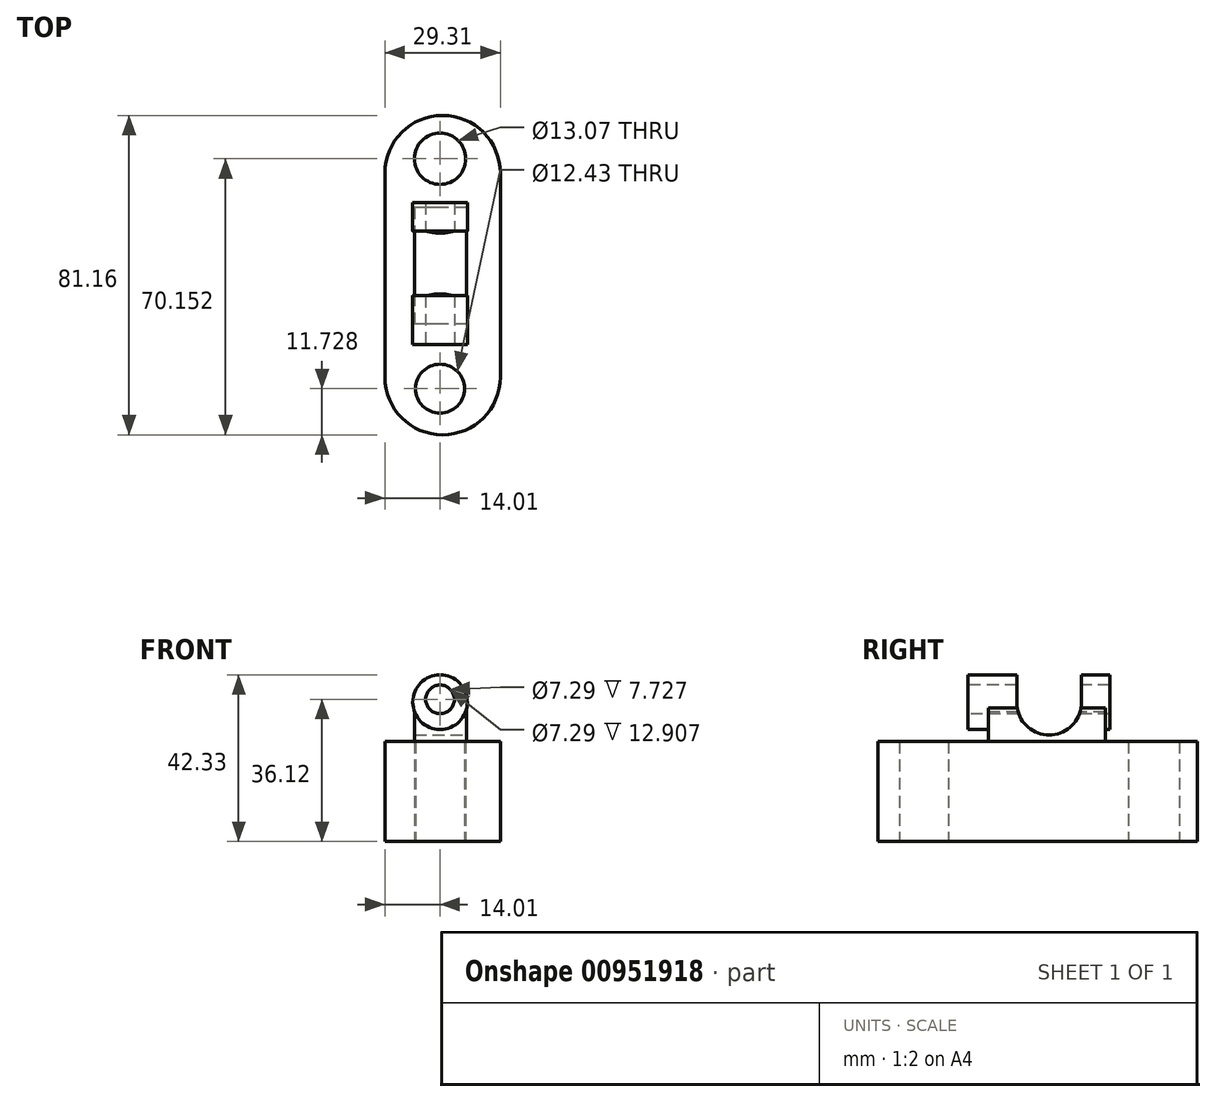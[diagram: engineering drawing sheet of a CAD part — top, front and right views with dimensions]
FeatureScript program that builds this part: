
annotation { "Feature Type Name" : "Feature", "Feature Type Description" : "" }
export const myFeature = defineFeature(function(context is Context, id is Id, definition is map)
    precondition{}
    {
        {
            var Q0;
            Q0=qCreatedBy(makeId("Top.planeOp"),FACE);
            var sketch = newSketch(context, id + "F0", { "sketchPlane" : qUnion([Q0])});
            skLineSegment(sketch, "E0.bottom", {"start": v(-14, -26.29) * mm, "end": v(15.3, -26.29) * mm});
            skLineSegment(sketch, "E0.top", {"start": v(-14, 25.56) * mm, "end": v(15.3, 25.56) * mm});
            skLineSegment(sketch, "E0.left", {"start": v(-14, -26.29) * mm, "end": v(-14, 25.56) * mm});
            skLineSegment(sketch, "E0.right", {"start": v(15.3, -26.29) * mm, "end": v(15.3, 25.56) * mm});
            skArc(sketch, "E1", {"start": v(-14, -26.29) * mm, "mid": v(0.64, -40.94) * mm, "end": v(15.3, -26.29) * mm});
            skArc(sketch, "E2", {"start": v(15.3, 25.56) * mm, "mid": v(0.64, 40.22) * mm, "end": v(-14, 25.56) * mm});
            skSolve(sketch);
        }
        {
            var Q0;
            Q0 = qSketchRegion(id + "F0", true);
            extrude(context, id + "F1", {"entities" : qUnion([Q0]), "depth" : 25.4 * mm, "offsetDistance" : 25.4 * mm});
        }
        {
            var Q0;
            Q0=qCreatedBy(makeId("Top.planeOp"),FACE);
            var sketch = newSketch(context, id + "F2", { "sketchPlane" : qUnion([Q0])});
            skCircle(sketch, "E3", {"center": v(0, -29.21) * mm, "radius": 6.21 * mm});
            skCircle(sketch, "E4", {"center": v(0, 29.21) * mm, "radius": 6.53 * mm});
            skSolve(sketch);
        }
        {
            var Q0;
            Q0=makeQuery(id+"F2.imprint","IMPRINT",FACE,{"disambiguationData":[TD([[makeQuery(id+"F2.imprint","IMPRINT",EDGE,{"derivedFrom":sQuery(id+"F2.wireOp",EDGE,"E3")}),1.0]])]});
            var Q1;
            Q1=makeQuery(id+"F2.imprint","IMPRINT",FACE,{"disambiguationData":[TD([[makeQuery(id+"F2.imprint","IMPRINT",EDGE,{"derivedFrom":sQuery(id+"F2.wireOp",EDGE,"E4")}),1.0]])]});
            extrude(context, id + "F3", {"entities" : qUnion([Q0, Q1]), "operationType" : NewBodyOperationType.REMOVE, "depth" : 73.9 * mm, "offsetDistance" : 25.4 * mm});
        }
        {
            var Q0;
            Q0=qCreatedBy(makeId("Top.planeOp"),FACE);
            var sketch = newSketch(context, id + "F4", { "sketchPlane" : qUnion([Q0])});
            skLineSegment(sketch, "E5.bottom", {"start": v(-6.48, -12.8) * mm, "end": v(6.76, -12.8) * mm});
            skLineSegment(sketch, "E5.top", {"start": v(-6.48, 16.84) * mm, "end": v(6.76, 16.84) * mm});
            skLineSegment(sketch, "E5.left", {"start": v(-6.48, -12.8) * mm, "end": v(-6.48, 16.84) * mm});
            skLineSegment(sketch, "E5.right", {"start": v(6.76, -12.8) * mm, "end": v(6.76, 16.84) * mm});
            skSolve(sketch);
        }
        {
            var Q0;
            Q0 = qSketchRegion(id + "F4", true);
            extrude(context, id + "F5", {"entities" : qUnion([Q0]), "operationType" : NewBodyOperationType.ADD, "depth" : 36.32 * mm, "offsetDistance" : 25.4 * mm});
        }
        {
            var Q0;
            Q0=qCreatedBy(makeId("Front.planeOp"),FACE);
            var sketch = newSketch(context, id + "F6", { "sketchPlane" : qUnion([Q0])});
            skCircle(sketch, "E6", {"center": v(0, 35.4) * mm, "radius": 6.93 * mm});
            skSolve(sketch);
        }
        {
            var Q0;
            Q0 = qSketchRegion(id + "F6", true);
            extrude(context, id + "F7", {"entities" : qUnion([Q0]), "operationType" : NewBodyOperationType.ADD, "oppositeDirection" : true, "depth" : 36.07 * mm, "offsetDistance" : 25.4 * mm, "symmetric" : true});
        }
        {
            var Q0;
            Q0=qCreatedBy(makeId("Right.planeOp"),FACE);
            var sketch = newSketch(context, id + "F8", { "sketchPlane" : qUnion([Q0])});
            skLineSegment(sketch, "E7.bottom", {"start": v(-5.61, 42.45) * mm, "end": v(10.8, 42.45) * mm});
            skLineSegment(sketch, "E7.top", {"start": v(-5.61, 35.26) * mm, "end": v(10.8, 35.26) * mm});
            skLineSegment(sketch, "E7.left", {"start": v(-5.61, 42.45) * mm, "end": v(-5.61, 35.26) * mm});
            skLineSegment(sketch, "E7.right", {"start": v(10.8, 42.45) * mm, "end": v(10.8, 35.26) * mm});
            skCircle(sketch, "E8", {"center": v(2.6, 35.26) * mm, "radius": 8.2 * mm});
            skSolve(sketch);
        }
        {
            var Q0;
            Q0 = qSketchRegion(id + "F8", true);
            extrude(context, id + "F9", {"entities" : qUnion([Q0]), "operationType" : NewBodyOperationType.REMOVE, "oppositeDirection" : true, "depth" : 49.78 * mm, "offsetDistance" : 25.4 * mm, "symmetric" : true});
        }
        {
            var Q0;
            Q0=qCreatedBy(makeId("Front.planeOp"),FACE);
            var sketch = newSketch(context, id + "F10", { "sketchPlane" : qUnion([Q0])});
            skCircle(sketch, "E9", {"center": v(0, 36.12) * mm, "radius": 3.64 * mm});
            skSolve(sketch);
        }
        {
            var Q0;
            Q0 = qSketchRegion(id + "F10", true);
            extrude(context, id + "F11", {"entities" : qUnion([Q0]), "operationType" : NewBodyOperationType.REMOVE, "oppositeDirection" : true, "depth" : 111.76 * mm, "offsetDistance" : 25.4 * mm, "symmetric" : true});
        }
    });
